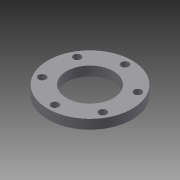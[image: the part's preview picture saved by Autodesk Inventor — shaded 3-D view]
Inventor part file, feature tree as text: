
AUTODESK INVENTOR PART (.ipt)
format: ipt  version: 2014 SP1 (Build 180222100, 222)  size: 96,768 bytes
history: native  units: in
note: dims shown in document units (in); Inventor stores cm internally (conversion verified against a paired STEP export)
features: extrude x2, sketch x2
ambient origin geometry x8: Origin, YZ Plane, XZ Plane, XY Plane, X Axis, Y Axis, Z Axis, Center Point
bodies: Solid1 (feature_tree)
feature tree (4):
  extrude  "Extrusion1"  Depth=1.25in
  extrude  "Extrusion2"  Depth=0.25in
  sketch  "Sketch1"  dims[d0=2.25in d1=1.25in]
  sketch  "Sketch2"  dims[d2=0.25in d3=0.0in d4=1.875in d5=0.204in d6=2.3622in d8=360.0deg d10=1.0in d11=0.0in]
